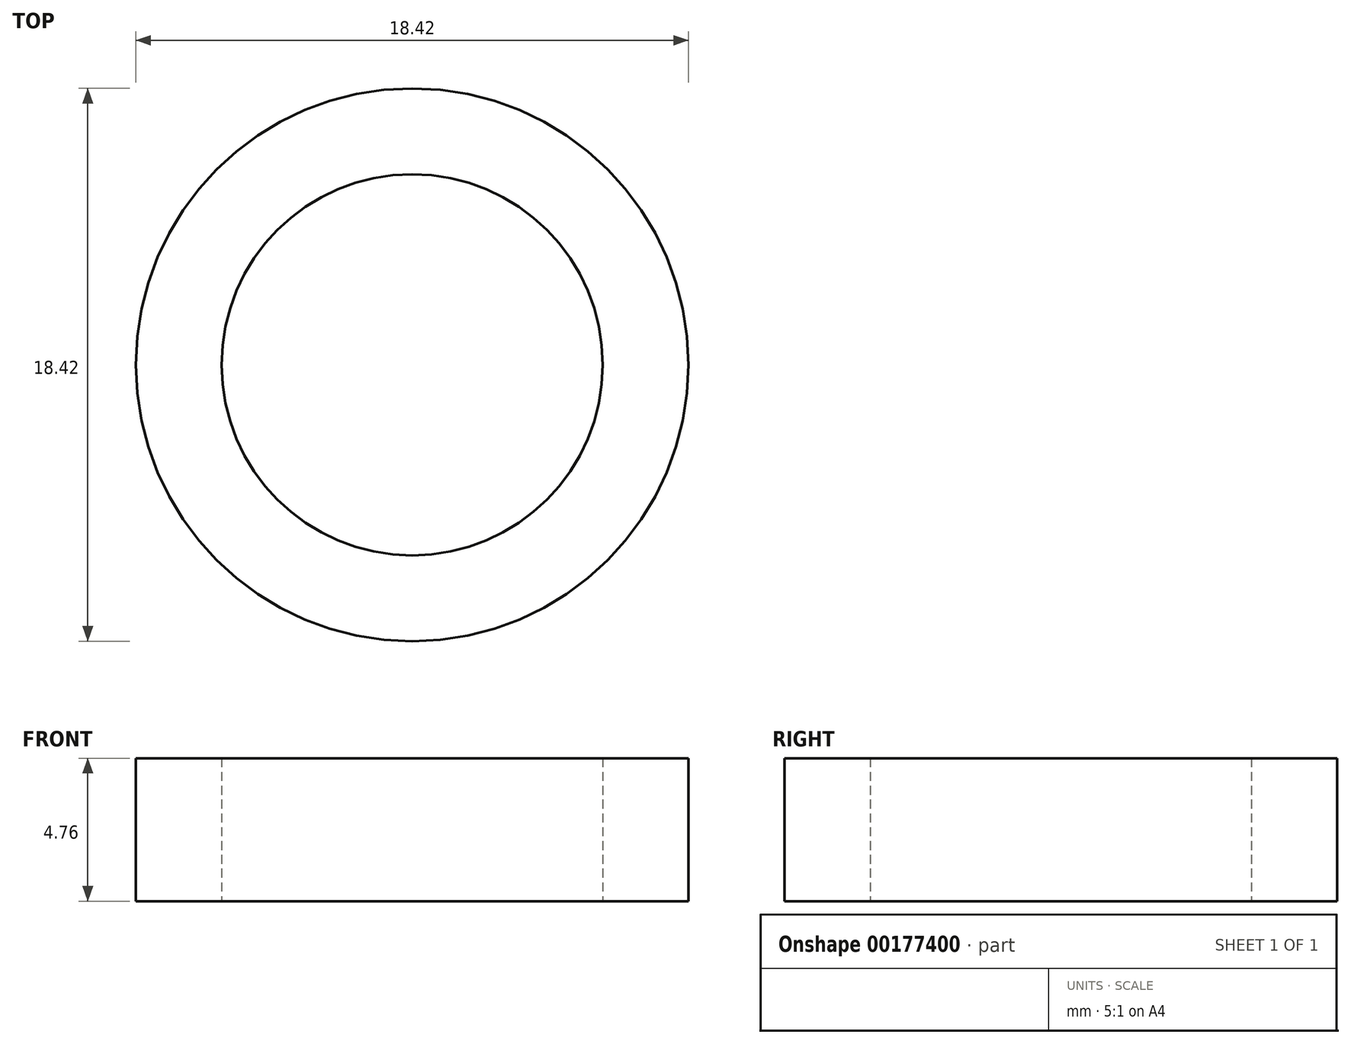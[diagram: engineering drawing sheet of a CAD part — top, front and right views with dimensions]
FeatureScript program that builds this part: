
annotation { "Feature Type Name" : "Feature", "Feature Type Description" : "" }
export const myFeature = defineFeature(function(context is Context, id is Id, definition is map)
    precondition{}
    {
        {
            var Q0;
            Q0=qCreatedBy(makeId("Top.planeOp"),FACE);
            var sketch = newSketch(context, id + "F0", { "sketchPlane" : qUnion([Q0])});
            skCircle(sketch, "E0", {"center": v(0, 0) * mm, "radius": 6.35 * mm});
            skCircle(sketch, "E1", {"center": v(0, 0) * mm, "radius": 9.2 * mm});
            skSolve(sketch);
        }
        {
            var Q0;
            Q0=makeQuery(id+"F0.imprint","IMPRINT",FACE,{"disambiguationData":[TD([[makeQuery(id+"F0.imprint","IMPRINT",EDGE,{"derivedFrom":sQuery(id+"F0.wireOp",EDGE,"E0")}),-1.0]])]});
            extrude(context, id + "F1", {"entities" : qUnion([Q0]), "depth" : 4.76 * mm});
        }
    });
